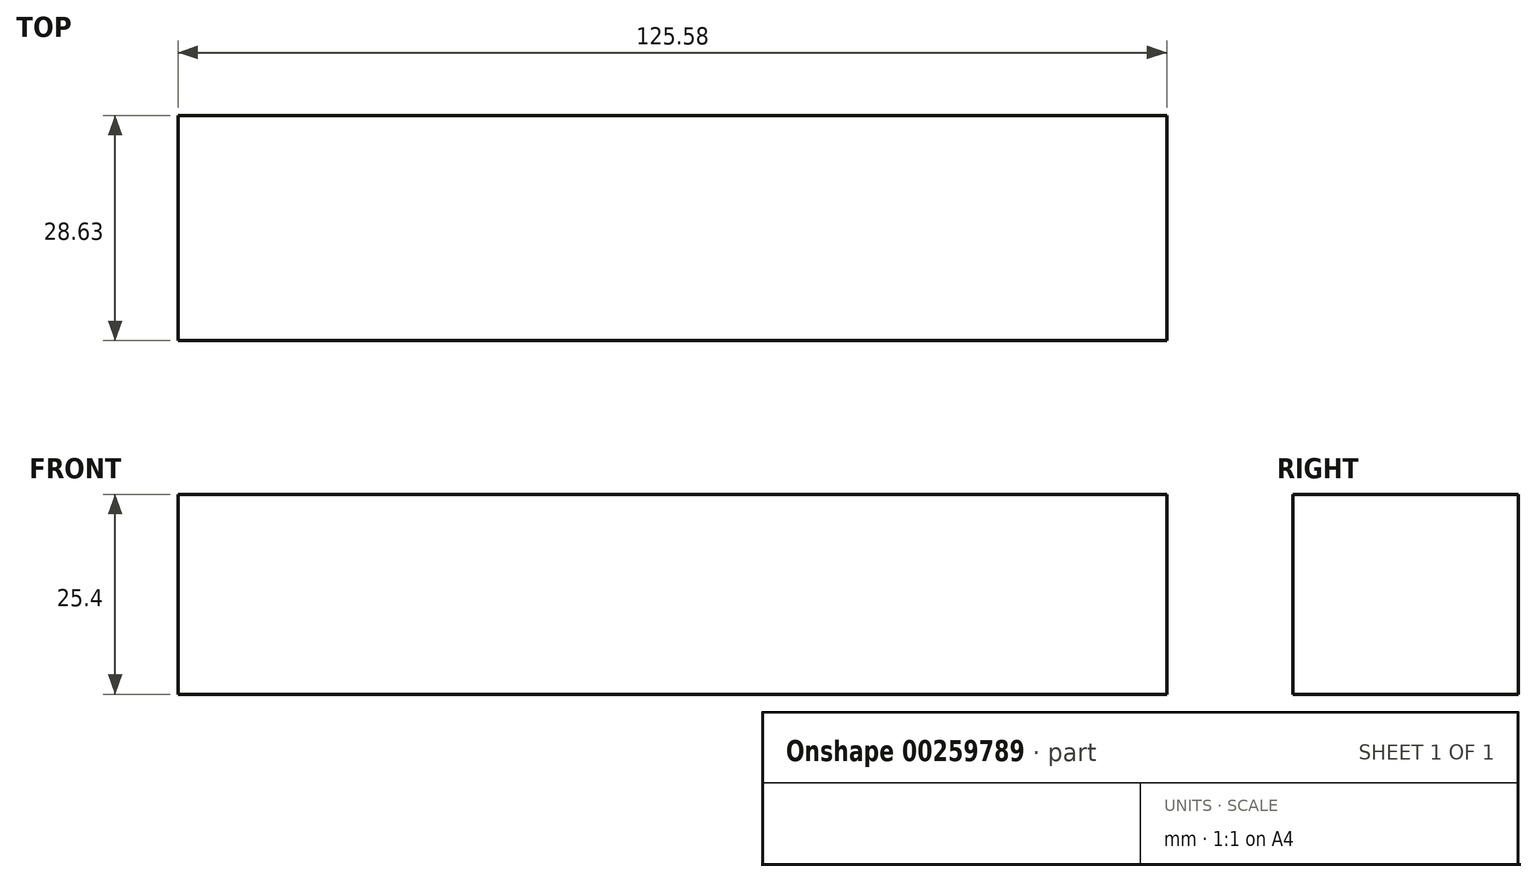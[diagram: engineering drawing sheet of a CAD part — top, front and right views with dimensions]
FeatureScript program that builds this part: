
annotation { "Feature Type Name" : "Feature", "Feature Type Description" : "" }
export const myFeature = defineFeature(function(context is Context, id is Id, definition is map)
    precondition{}
    {
        {
            var Q0;
            Q0=qCreatedBy(makeId("Top.planeOp"),FACE);
            var sketch = newSketch(context, id + "F0", { "sketchPlane" : qUnion([Q0])});
            skLineSegment(sketch, "E0.bottom", {"start": v(-60.95, 16.36) * mm, "end": v(64.63, 16.36) * mm});
            skLineSegment(sketch, "E0.top", {"start": v(-60.95, -12.27) * mm, "end": v(64.63, -12.27) * mm});
            skLineSegment(sketch, "E0.left", {"start": v(-60.95, 16.36) * mm, "end": v(-60.95, -12.27) * mm});
            skLineSegment(sketch, "E0.right", {"start": v(64.63, 16.36) * mm, "end": v(64.63, -12.27) * mm});
            skSolve(sketch);
        }
        {
            var Q0;
            Q0 = qSketchRegion(id + "F0", true);
            extrude(context, id + "F1", {"entities" : qUnion([Q0]), "depth" : 25.4 * mm});
        }
    });
